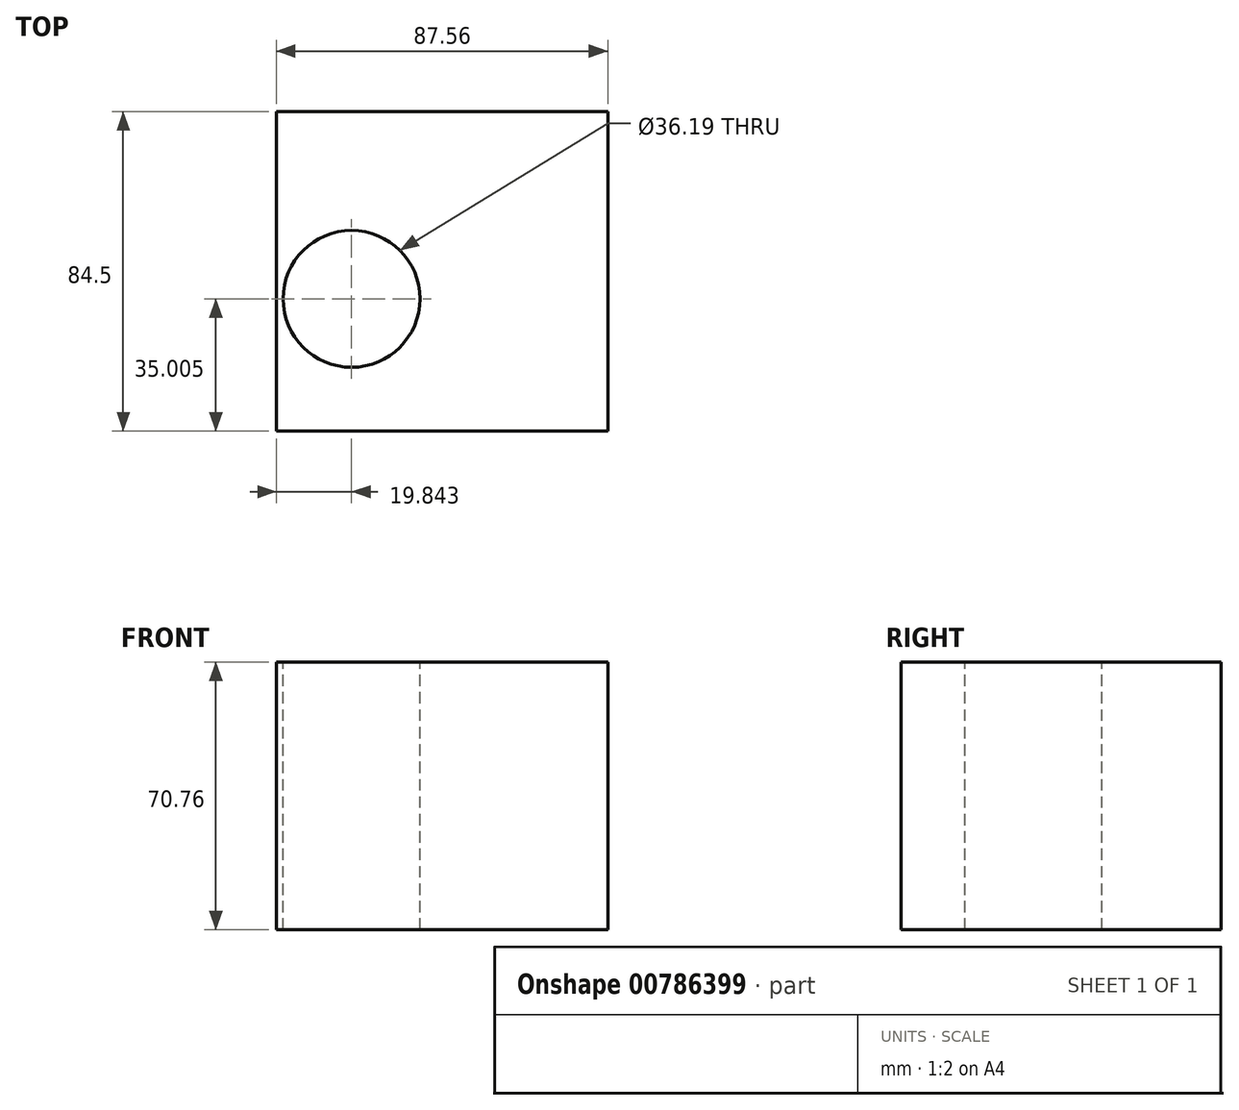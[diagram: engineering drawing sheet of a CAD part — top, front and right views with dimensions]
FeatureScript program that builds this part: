
annotation { "Feature Type Name" : "Feature", "Feature Type Description" : "" }
export const myFeature = defineFeature(function(context is Context, id is Id, definition is map)
    precondition{}
    {
        {
            var Q0;
            Q0=qCreatedBy(makeId("Front.planeOp"),FACE);
            var sketch = newSketch(context, id + "F0", { "sketchPlane" : qUnion([Q0])});
            skLineSegment(sketch, "E0.bottom", {"start": v(-58.05, 45.26) * mm, "end": v(29.5, 45.26) * mm});
            skLineSegment(sketch, "E0.top", {"start": v(-58.05, -25.5) * mm, "end": v(29.5, -25.5) * mm});
            skLineSegment(sketch, "E0.left", {"start": v(-58.05, 45.26) * mm, "end": v(-58.05, -25.5) * mm});
            skLineSegment(sketch, "E0.right", {"start": v(29.5, 45.26) * mm, "end": v(29.5, -25.5) * mm});
            skLineSegment(sketch, "E1.bottom", {"start": v(-20.87, 7.44) * mm, "end": v(68.84, 7.44) * mm});
            skLineSegment(sketch, "E1.top", {"start": v(-20.87, -60.92) * mm, "end": v(68.84, -60.92) * mm});
            skLineSegment(sketch, "E1.left", {"start": v(-20.87, 7.44) * mm, "end": v(-20.87, -60.92) * mm});
            skLineSegment(sketch, "E1.right", {"start": v(68.84, 7.44) * mm, "end": v(68.84, -60.92) * mm});
            skSolve(sketch);
        }
        {
            var Q0;
            {var subQ0=sQuery(id+"F0.wireOp",EDGE,"E0.right");var subQ1=sQuery(id+"F0.wireOp",EDGE,"E0.top");var subQ2=makeQuery(id+"F0.imprint","INTERSECT",VERTEX,{"derivedFrom":[subQ1,subQ0]});Q0=makeQuery(id+"F0.imprint","IMPRINT",FACE,{"disambiguationData":[TD([[makeQuery(id+"F0.imprint","IMPRINT",EDGE,{"disambiguationData":[TD([[subQ2,1.0]])],"derivedFrom":subQ1}),1.0]])]});}
            var Q1;
            {var subQ1=sQuery(id+"F0.wireOp",EDGE,"E0.bottom");Q1=makeQuery(id+"F0.imprint","IMPRINT",FACE,{"disambiguationData":[TD([[makeQuery(id+"F0.imprint","IMPRINT",EDGE,{"derivedFrom":subQ1}),-1.0]])]});}
            extrude(context, id + "F1", {"entities" : qUnion([Q0, Q1]), "depth" : 84.5 * mm, "offsetDistance" : 25 * mm});
        }
        {
            var Q0;
            Q0=makeQuery(id+"F1.opExtrude","SWEPT_FACE",FACE,{"disambiguationData":[OSD([sQuery(id+"F0.wireOp",EDGE,"E0.bottom")])]});
            var sketch = newSketch(context, id + "F2", { "sketchPlane" : qUnion([Q0])});
            skCircle(sketch, "E2", {"center": v(-38.2, -49.5) * mm, "radius": 18.1 * mm});
            skSolve(sketch);
        }
        {
            var Q0;
            Q0 = qSketchRegion(id + "F2", true);
            extrude(context, id + "F3", {"entities" : qUnion([Q0]), "operationType" : NewBodyOperationType.REMOVE, "endBound" : BoundingType.THROUGH_ALL, "oppositeDirection" : true, "depth" : 25 * mm, "offsetDistance" : 25 * mm});
        }
    });
